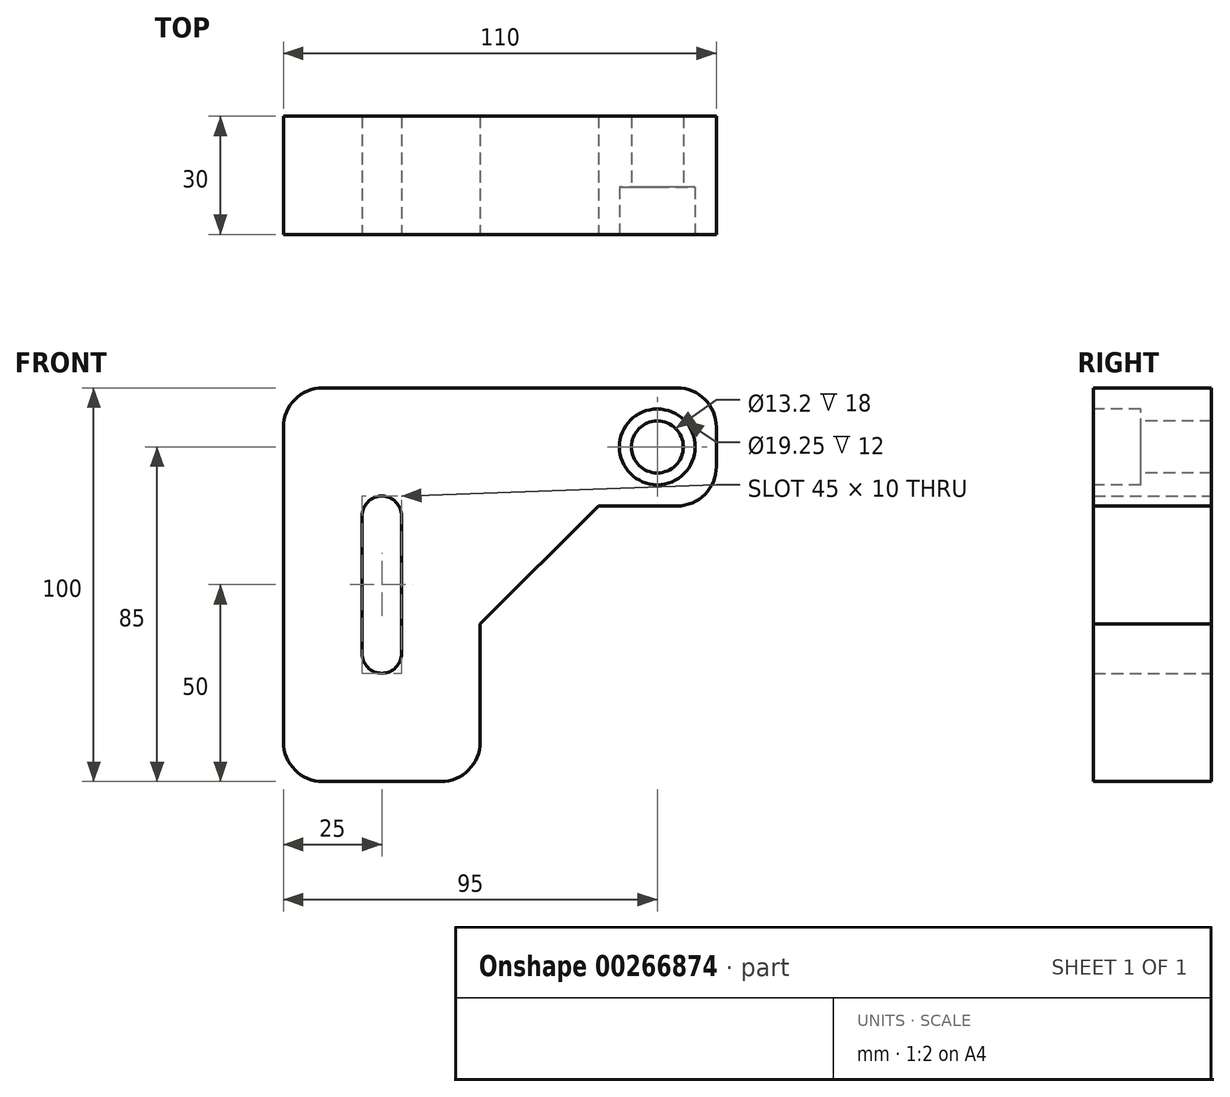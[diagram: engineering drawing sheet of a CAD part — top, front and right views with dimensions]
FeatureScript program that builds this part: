
annotation { "Feature Type Name" : "Feature", "Feature Type Description" : "" }
export const myFeature = defineFeature(function(context is Context, id is Id, definition is map)
    precondition{}
    {
        {
            var Q0;
            Q0=qCreatedBy(makeId("Front.planeOp"),FACE);
            var sketch = newSketch(context, id + "F0", { "sketchPlane" : qUnion([Q0])});
            skLineSegment(sketch, "E0", {"start": v(0, 0) * mm, "end": v(0, 100) * mm});
            skLineSegment(sketch, "E1", {"start": v(0, 100) * mm, "end": v(110, 100) * mm});
            skLineSegment(sketch, "E2", {"start": v(110, 100) * mm, "end": v(110, 70) * mm});
            skLineSegment(sketch, "E3", {"start": v(110, 70) * mm, "end": v(80, 70) * mm});
            skLineSegment(sketch, "E4", {"start": v(80, 70) * mm, "end": v(50, 40) * mm});
            skLineSegment(sketch, "E5", {"start": v(50, 40) * mm, "end": v(50, 0) * mm});
            skLineSegment(sketch, "E6", {"start": v(50, 0) * mm, "end": v(0, 0) * mm});
            skPoint(sketch, "E7", {"position": v(95, 85) * mm});
            skPoint(sketch, "E7.positionSnap0", {"position": v(95, 70) * mm});
            skSolve(sketch);
        }
        {
            var Q0;
            Q0=makeQuery(id+"F0.imprint","IMPRINT",FACE,{"disambiguationData":[TD([[makeQuery(id+"F0.imprint","IMPRINT",EDGE,{"derivedFrom":sQuery(id+"F0.wireOp",EDGE,"E0")}),-1.0]])]});
            extrude(context, id + "F1", {"entities" : qUnion([Q0]), "oppositeDirection" : true, "depth" : 30 * mm});
        }
        {
            var Q0;
            Q0=makeQuery(id+"F1.opExtrude","CAP_FACE",FACE,{"disambiguationData":[OSD([sQuery(id+"F0.wireOp",EDGE,"E0"),sQuery(id+"F0.wireOp",EDGE,"E1"),sQuery(id+"F0.wireOp",EDGE,"E2"),sQuery(id+"F0.wireOp",EDGE,"E3"),sQuery(id+"F0.wireOp",EDGE,"E4"),sQuery(id+"F0.wireOp",EDGE,"E5"),sQuery(id+"F0.wireOp",EDGE,"E6")])],"isStart":true});
            var sketch = newSketch(context, id + "F2", { "sketchPlane" : qUnion([Q0])});
            skPoint(sketch, "E8", {"position": v(95, 85) * mm});
            skSolve(sketch);
        }
        {
            var Q0;
            Q0=sQuery(id+"F2.wireOp",VERTEX,"E8");
            var Q1;
            Q1=makeQuery(id+"F1.opExtrude","SWEPT_BODY",BODY,{"disambiguationData":[OSD([sQuery(id+"F0.wireOp",EDGE,"E0"),sQuery(id+"F0.wireOp",EDGE,"E1"),sQuery(id+"F0.wireOp",EDGE,"E2"),sQuery(id+"F0.wireOp",EDGE,"E3"),sQuery(id+"F0.wireOp",EDGE,"E4"),sQuery(id+"F0.wireOp",EDGE,"E5"),sQuery(id+"F0.wireOp",EDGE,"E6")])]});
            hole(context, id + "F3", {"style" : HoleStyle.C_BORE, "endStyle" : HoleEndStyle.THROUGH, "standardTappedOrClearance" : lookupTablePath({ "standard" : "ISO", "fit" : "Normal", "size" : "M12", "type" : "Clearance" }), "standardBlindInLast" : lookupTablePath({ "fit" : "Standard", "standard" : "ISO", "size" : "M12", "type" : "Clearance" }), "holeDiameter" : 13.2 * mm, "cBoreDiameter" : 19.25 * mm, "cBoreDepth" : 12 * mm, "tappedDepth" : 12 * mm, "tapClearance" : 3, "locations" : qUnion([Q0]), "scope" : qUnion([Q1])});
        }
        {
            var Q0;
            Q0=makeQuery(id+"F1.opExtrude","SWEPT_EDGE",EDGE,{"disambiguationData":[OSD([sQuery(id+"F0.wireOp",EDGE,"E0"),sQuery(id+"F0.wireOp",EDGE,"E1")])]});
            var Q1;
            Q1=makeQuery(id+"F1.opExtrude","SWEPT_EDGE",EDGE,{"disambiguationData":[OSD([sQuery(id+"F0.wireOp",EDGE,"E5"),sQuery(id+"F0.wireOp",EDGE,"E6")])]});
            var Q2;
            Q2=makeQuery(id+"F1.opExtrude","SWEPT_EDGE",EDGE,{"disambiguationData":[OSD([sQuery(id+"F0.wireOp",EDGE,"E2"),sQuery(id+"F0.wireOp",EDGE,"E3")])]});
            var Q3;
            Q3=makeQuery(id+"F1.opExtrude","SWEPT_EDGE",EDGE,{"disambiguationData":[OSD([sQuery(id+"F0.wireOp",EDGE,"E1"),sQuery(id+"F0.wireOp",EDGE,"E2")])]});
            var Q4;
            Q4=makeQuery(id+"F1.opExtrude","SWEPT_EDGE",EDGE,{"disambiguationData":[OSD([sQuery(id+"F0.wireOp",EDGE,"E0"),sQuery(id+"F0.wireOp",EDGE,"E6")])]});
            fillet(context, id + "F4", {"entities" : qUnion([Q0, Q1, Q2, Q3, Q4]), "radius" : 10 * mm, "tangentPropagation" : true, "allowEdgeOverflow" : false});
        }
        {
            var Q0;
            Q0=makeQuery(id+"F1.opExtrude","CAP_FACE",FACE,{"disambiguationData":[OSD([sQuery(id+"F0.wireOp",EDGE,"E0"),sQuery(id+"F0.wireOp",EDGE,"E1"),sQuery(id+"F0.wireOp",EDGE,"E2"),sQuery(id+"F0.wireOp",EDGE,"E3"),sQuery(id+"F0.wireOp",EDGE,"E4"),sQuery(id+"F0.wireOp",EDGE,"E5"),sQuery(id+"F0.wireOp",EDGE,"E6")])],"isStart":true});
            var sketch = newSketch(context, id + "F5", { "sketchPlane" : qUnion([Q0])});
            skLineSegment(sketch, "E9", {"start": v(20, 72.5) * mm, "end": v(20, 27.5) * mm});
            skLineSegment(sketch, "E10", {"start": v(20, 27.5) * mm, "end": v(30, 27.5) * mm});
            skLineSegment(sketch, "E11", {"start": v(30, 27.5) * mm, "end": v(30, 72.5) * mm});
            skLineSegment(sketch, "E12", {"start": v(30, 72.5) * mm, "end": v(20, 72.5) * mm});
            skSolve(sketch);
        }
        {
            var Q0;
            Q0 = qSketchRegion(id + "F5", true);
            extrude(context, id + "F6", {"entities" : qUnion([Q0]), "operationType" : NewBodyOperationType.REMOVE, "endBound" : BoundingType.THROUGH_ALL, "oppositeDirection" : true, "depth" : 10 * mm});
        }
        {
            var Q0;
            Q0=makeQuery(id+"F6.boolean.opBoolean","COPY",EDGE,{"derivedFrom":makeQuery(id+"F6.opExtrude","SWEPT_EDGE",EDGE,{"disambiguationData":[OSD([sQuery(id+"F5.wireOp",EDGE,"E9"),sQuery(id+"F5.wireOp",EDGE,"E12")])]})});
            var Q1;
            Q1=makeQuery(id+"F6.boolean.opBoolean","COPY",EDGE,{"derivedFrom":makeQuery(id+"F6.opExtrude","SWEPT_EDGE",EDGE,{"disambiguationData":[OSD([sQuery(id+"F5.wireOp",EDGE,"E11"),sQuery(id+"F5.wireOp",EDGE,"E12")])]})});
            var Q2;
            Q2=makeQuery(id+"F6.boolean.opBoolean","COPY",EDGE,{"derivedFrom":makeQuery(id+"F6.opExtrude","SWEPT_EDGE",EDGE,{"disambiguationData":[OSD([sQuery(id+"F5.wireOp",EDGE,"E10"),sQuery(id+"F5.wireOp",EDGE,"E11")])]})});
            var Q3;
            Q3=makeQuery(id+"F6.boolean.opBoolean","COPY",EDGE,{"derivedFrom":makeQuery(id+"F6.opExtrude","SWEPT_EDGE",EDGE,{"disambiguationData":[OSD([sQuery(id+"F5.wireOp",EDGE,"E9"),sQuery(id+"F5.wireOp",EDGE,"E10")])]})});
            fillet(context, id + "F7", {"entities" : qUnion([Q0, Q1, Q2, Q3]), "radius" : 5 * mm, "tangentPropagation" : true, "allowEdgeOverflow" : false});
        }
    });
